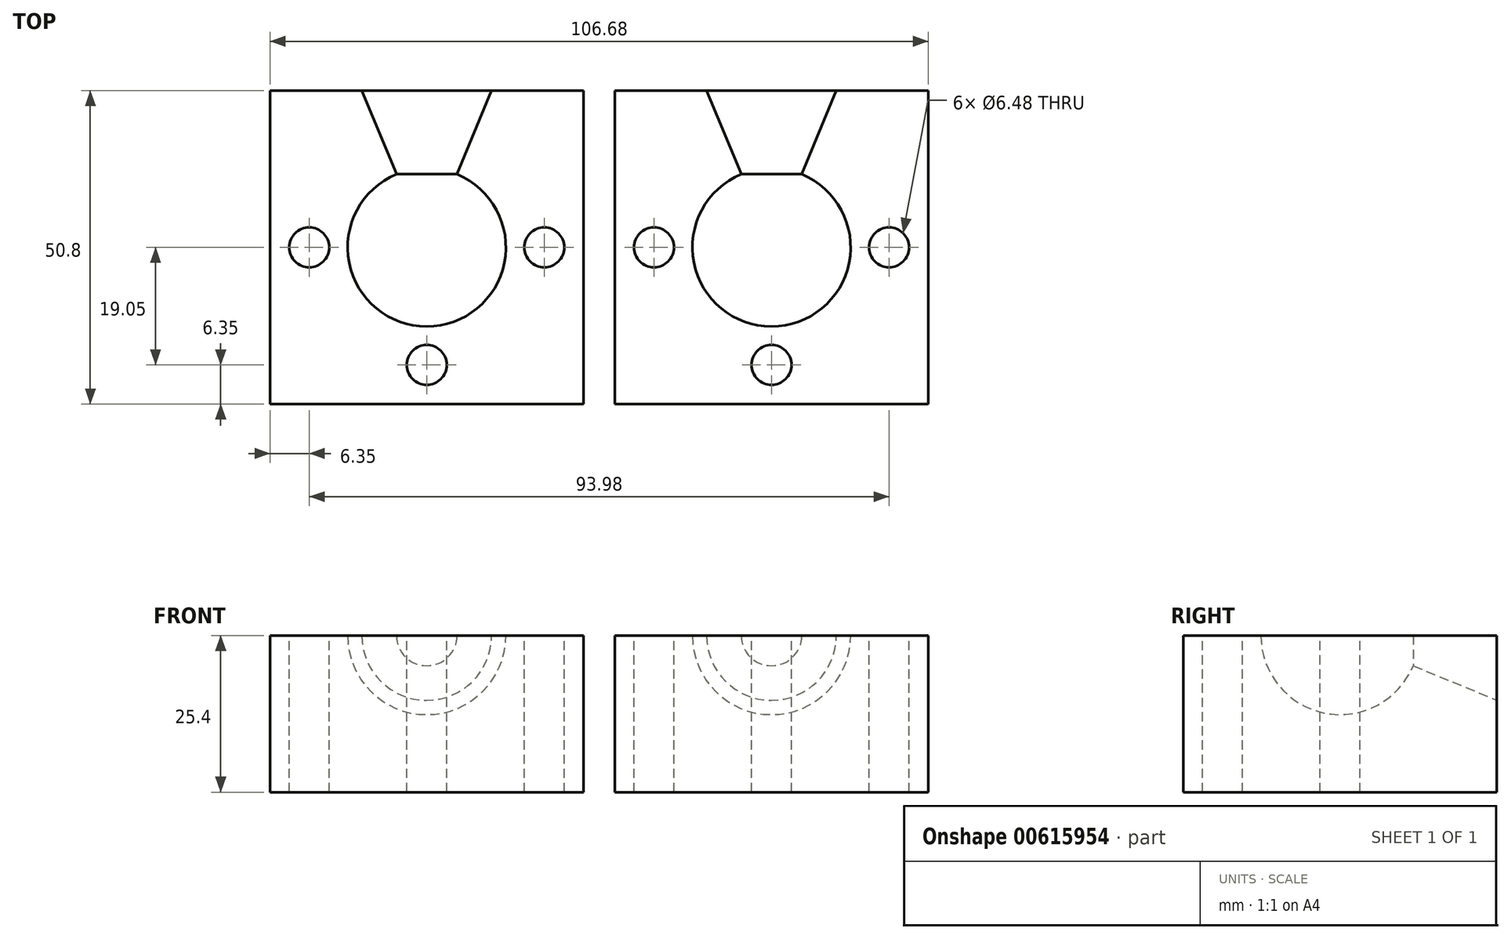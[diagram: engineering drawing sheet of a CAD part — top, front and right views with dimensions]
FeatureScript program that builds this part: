
annotation { "Feature Type Name" : "Feature", "Feature Type Description" : "" }
export const myFeature = defineFeature(function(context is Context, id is Id, definition is map)
    precondition{}
    {
        {
            var Q0;
            Q0=qCreatedBy(makeId("Top.planeOp"),FACE);
            var sketch = newSketch(context, id + "F0", { "sketchPlane" : qUnion([Q0])});
            skLineSegment(sketch, "E0.bottom", {"start": v(25.4, -25.4) * mm, "end": v(-25.4, -25.4) * mm});
            skLineSegment(sketch, "E0.top", {"start": v(25.4, 25.4) * mm, "end": v(-25.4, 25.4) * mm});
            skLineSegment(sketch, "E0.left", {"start": v(25.4, -25.4) * mm, "end": v(25.4, 25.4) * mm});
            skLineSegment(sketch, "E0.right", {"start": v(-25.4, -25.4) * mm, "end": v(-25.4, 25.4) * mm});
            skPoint(sketch, "E0.middle", {"position": v(0, 0) * mm});
            skSolve(sketch);
        }
        {
            var Q0;
            Q0=makeQuery(id+"F0.imprint","IMPRINT",FACE,{"disambiguationData":[TD([[makeQuery(id+"F0.imprint","IMPRINT",EDGE,{"derivedFrom":sQuery(id+"F0.wireOp",EDGE,"E0.bottom")}),-1.0]])]});
            extrude(context, id + "F1", {"entities" : qUnion([Q0]), "depth" : 25.4 * mm, "offsetDistance" : 25.4 * mm});
        }
        {
            var Q0;
            Q0=makeQuery(id+"F1.opExtrude","CAP_FACE",FACE,{"disambiguationData":[OSD([sQuery(id+"F0.wireOp",EDGE,"E0.bottom"),sQuery(id+"F0.wireOp",EDGE,"E0.top"),sQuery(id+"F0.wireOp",EDGE,"E0.left"),sQuery(id+"F0.wireOp",EDGE,"E0.right")])],"isStart":false});
            var sketch = newSketch(context, id + "F2", { "sketchPlane" : qUnion([Q0])});
            skArc(sketch, "E1", {"start": v(0, -12.83) * mm, "mid": v(12.83, 0) * mm, "end": v(0, 12.83) * mm});
            skLineSegment(sketch, "E2", {"start": v(0, 0) * mm, "end": v(0, 12.83) * mm});
            skLineSegment(sketch, "E3", {"start": v(0, 12.83) * mm, "end": v(0, -12.83) * mm});
            skSolve(sketch);
        }
        {
            var Q0;
            Q0 = qSketchRegion(id + "F2", true);
            var Q1;
            Q1=sQuery(id+"F2.wireOp",EDGE,"E3");
            revolve(context, id + "F3", {"operationType" : NewBodyOperationType.REMOVE, "entities" : qUnion([Q0]), "axis" : qUnion([Q1]), "revolveType" : RevolveType.FULL, "oppositeDirection" : true});
        }
        {
            var Q0;
            Q0=makeQuery(id+"F1.opExtrude","CAP_FACE",FACE,{"disambiguationData":[OSD([sQuery(id+"F0.wireOp",EDGE,"E0.bottom"),sQuery(id+"F0.wireOp",EDGE,"E0.top"),sQuery(id+"F0.wireOp",EDGE,"E0.left"),sQuery(id+"F0.wireOp",EDGE,"E0.right")])],"isStart":false});
            var sketch = newSketch(context, id + "F4", { "sketchPlane" : qUnion([Q0])});
            skLineSegment(sketch, "E4", {"start": v(0, 0) * mm, "end": v(10.51, 25.4) * mm});
            skLineSegment(sketch, "E5", {"start": v(10.51, 25.4) * mm, "end": v(0, 25.4) * mm});
            skLineSegment(sketch, "E6", {"start": v(0, 25.4) * mm, "end": v(0, 0) * mm});
            skSolve(sketch);
        }
        {
            var Q0;
            {var subQ0=sQuery(id+"F4.wireOp",EDGE,"E5");Q0=makeQuery(id+"F4.imprint","IMPRINT",FACE,{"disambiguationData":[TD([[makeQuery(id+"F4.imprint","IMPRINT",EDGE,{"derivedFrom":subQ0}),1.0]])]});}
            var Q1;
            Q1=sQuery(id+"F4.wireOp",EDGE,"E6");
            revolve(context, id + "F5", {"operationType" : NewBodyOperationType.REMOVE, "entities" : qUnion([Q0]), "axis" : qUnion([Q1]), "revolveType" : RevolveType.FULL, "oppositeDirection" : true});
        }
        {
            var Q0;
            Q0=makeQuery(id+"F1.opExtrude","CAP_FACE",FACE,{"disambiguationData":[OSD([sQuery(id+"F0.wireOp",EDGE,"E0.bottom"),sQuery(id+"F0.wireOp",EDGE,"E0.top"),sQuery(id+"F0.wireOp",EDGE,"E0.left"),sQuery(id+"F0.wireOp",EDGE,"E0.right")])],"isStart":false});
            var sketch = newSketch(context, id + "F6", { "sketchPlane" : qUnion([Q0])});
            skLineSegment(sketch, "E7", {"start": v(0, 0) * mm, "end": v(19.05, 0) * mm});
            skLineSegment(sketch, "E8", {"start": v(19.05, 0) * mm, "end": v(0, 0) * mm});
            skLineSegment(sketch, "E9", {"start": v(0, 0) * mm, "end": v(-19.05, 0) * mm});
            skLineSegment(sketch, "E10", {"start": v(-19.05, 0) * mm, "end": v(0, 0) * mm});
            skLineSegment(sketch, "E11", {"start": v(0, 0) * mm, "end": v(0, -19.05) * mm});
            skPoint(sketch, "E11.endSnap0", {"position": v(0, -12.83) * mm});
            skSolve(sketch);
        }
        {
            var Q0;
            Q0=sQuery(id+"F6.wireOp",VERTEX,"E8.start");
            var Q1;
            Q1=sQuery(id+"F6.wireOp",VERTEX,"E11.end");
            var Q2;
            Q2=sQuery(id+"F6.wireOp",VERTEX,"E10.start");
            var Q3;
            Q3=makeQuery(id+"F1.opExtrude","SWEPT_BODY",BODY,{"disambiguationData":[OSD([sQuery(id+"F0.wireOp",EDGE,"E0.bottom"),sQuery(id+"F0.wireOp",EDGE,"E0.top"),sQuery(id+"F0.wireOp",EDGE,"E0.left"),sQuery(id+"F0.wireOp",EDGE,"E0.right")])]});
            hole(context, id + "F7", {"style" : HoleStyle.SIMPLE, "endStyle" : HoleEndStyle.THROUGH, "holeDiameter" : 6.48 * mm, "majorDiameter" : 6.35 * mm, "isTappedThrough" : true, "tappedDepth" : 12.7 * mm, "tapClearance" : 3, "locations" : qUnion([Q0, Q1, Q2]), "scope" : qUnion([Q3])});
        }
        {
            var Q0;
            Q0=makeQuery(id+"F1.opExtrude","SWEPT_BODY",BODY,{"disambiguationData":[OSD([sQuery(id+"F0.wireOp",EDGE,"E0.bottom"),sQuery(id+"F0.wireOp",EDGE,"E0.top"),sQuery(id+"F0.wireOp",EDGE,"E0.left"),sQuery(id+"F0.wireOp",EDGE,"E0.right")])]});
            transform(context, id + "F8", {"entities" : qUnion([Q0]), "transformType" : TransformType.TRANSLATION_3D, "dx" : -27.94 * mm, "dy" : 0 * mm, "dz" : 0 * mm, "makeCopy" : false});
        }
        {
            var Q0;
            Q0=makeQuery(id+"F1.opExtrude","SWEPT_BODY",BODY,{"disambiguationData":[OSD([sQuery(id+"F0.wireOp",EDGE,"E0.bottom"),sQuery(id+"F0.wireOp",EDGE,"E0.top"),sQuery(id+"F0.wireOp",EDGE,"E0.left"),sQuery(id+"F0.wireOp",EDGE,"E0.right")])]});
            transform(context, id + "F9", {"entities" : qUnion([Q0]), "transformType" : TransformType.TRANSLATION_3D, "dx" : 55.88 * mm, "dy" : 0 * mm, "dz" : 0 * mm, "makeCopy" : true});
        }
    });
